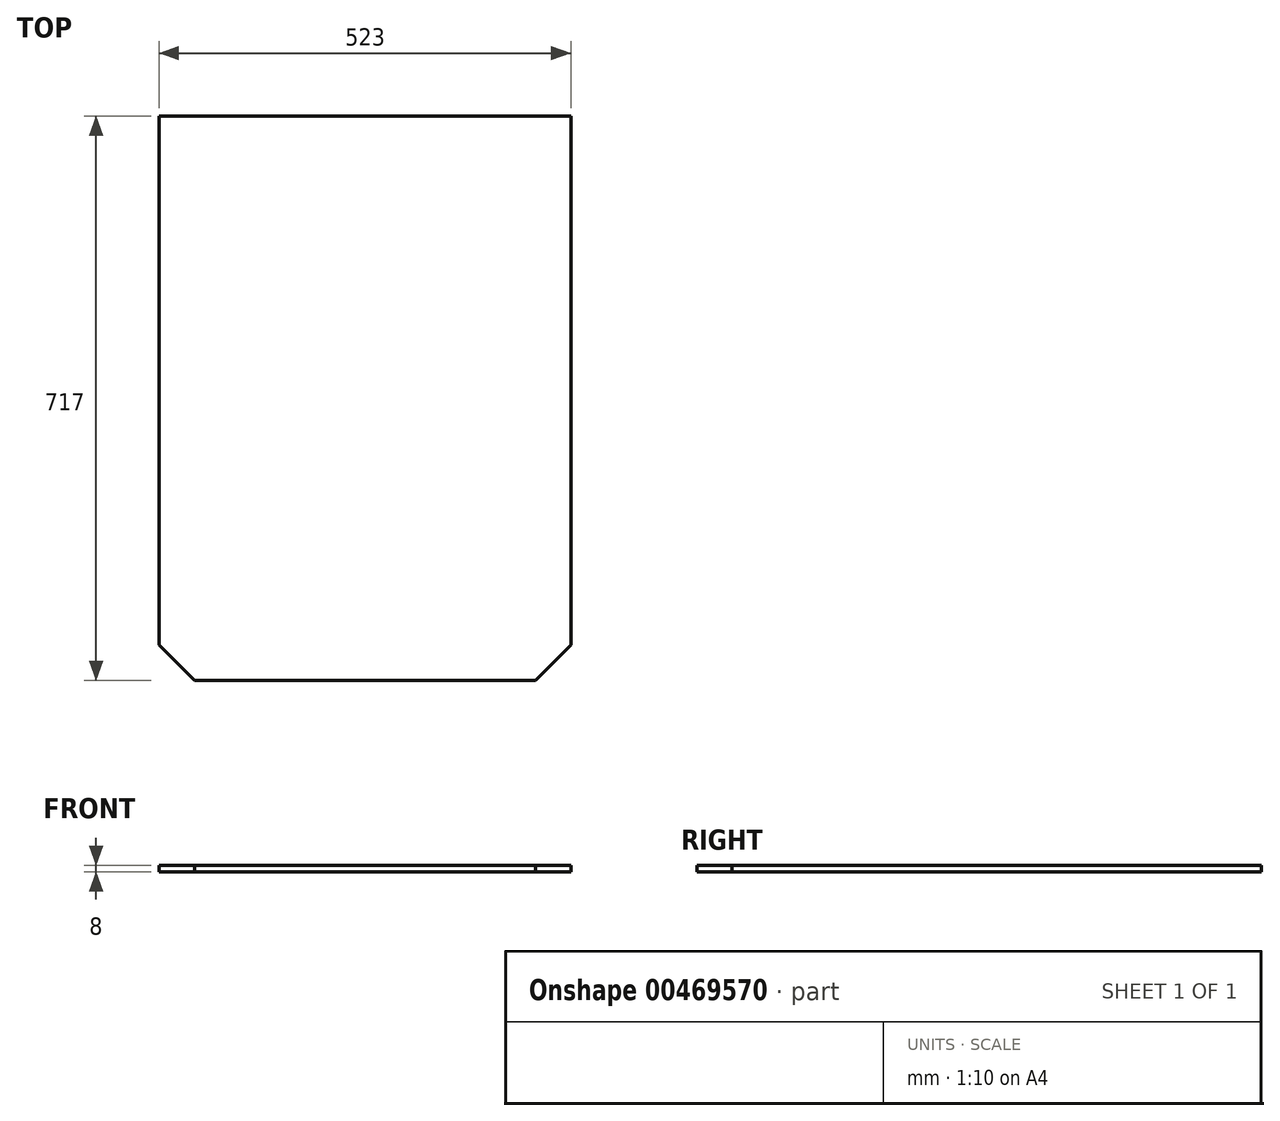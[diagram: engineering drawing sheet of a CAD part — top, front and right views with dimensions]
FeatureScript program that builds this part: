
annotation { "Feature Type Name" : "Feature", "Feature Type Description" : "" }
export const myFeature = defineFeature(function(context is Context, id is Id, definition is map)
    precondition{}
    {
        {
            var Q0;
            Q0=qCreatedBy(makeId("Top.planeOp"),FACE);
            var sketch = newSketch(context, id + "F0", { "sketchPlane" : qUnion([Q0])});
            skLineSegment(sketch, "E0", {"start": v(261.5, 363.98) * mm, "end": v(261.5, -308.02) * mm});
            skLineSegment(sketch, "E1", {"start": v(261.5, -308.02) * mm, "end": v(216.5, -353.02) * mm});
            skLineSegment(sketch, "E2", {"start": v(216.5, -353.02) * mm, "end": v(-216.5, -353.02) * mm});
            skLineSegment(sketch, "E3", {"start": v(-216.5, -353.02) * mm, "end": v(-261.5, -308.02) * mm});
            skLineSegment(sketch, "E4", {"start": v(-261.5, -308.02) * mm, "end": v(-261.5, 363.98) * mm});
            skLineSegment(sketch, "E5", {"start": v(-261.5, 363.98) * mm, "end": v(261.5, 363.98) * mm});
            skSolve(sketch);
        }
        {
            var Q0;
            Q0=makeQuery(id+"F0.imprint","IMPRINT",FACE,{"disambiguationData":[TD([[makeQuery(id+"F0.imprint","IMPRINT",EDGE,{"derivedFrom":sQuery(id+"F0.wireOp",EDGE,"E0")}),-1.0]])]});
            extrude(context, id + "F1", {"entities" : qUnion([Q0]), "depth" : 8 * mm});
        }
    });
